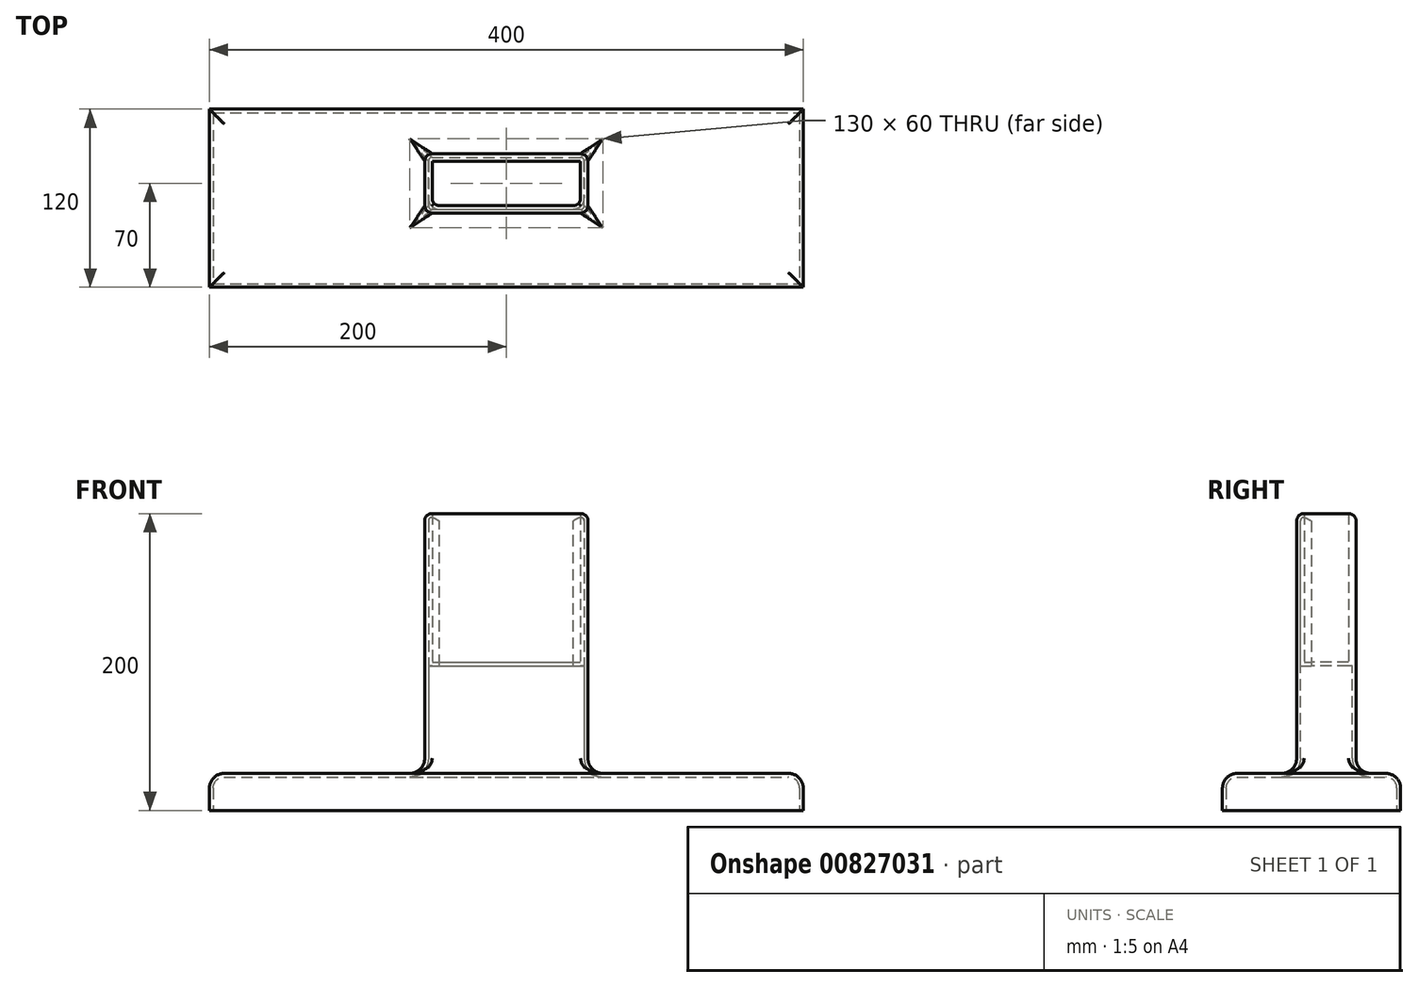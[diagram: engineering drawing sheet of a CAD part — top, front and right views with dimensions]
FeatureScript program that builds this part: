
annotation { "Feature Type Name" : "Feature", "Feature Type Description" : "" }
export const myFeature = defineFeature(function(context is Context, id is Id, definition is map)
    precondition{}
    {
        {
            var Q0;
            Q0=qCreatedBy(makeId("Front.planeOp"),FACE);
            var sketch = newSketch(context, id + "F0", { "sketchPlane" : qUnion([Q0])});
            skLineSegment(sketch, "E0.bottom", {"start": v(-55, 100) * mm, "end": v(55, 100) * mm});
            skLineSegment(sketch, "E0.top", {"start": v(-55, -100) * mm, "end": v(55, -100) * mm});
            skLineSegment(sketch, "E0.left", {"start": v(-55, 100) * mm, "end": v(-55, -100) * mm});
            skLineSegment(sketch, "E0.right", {"start": v(55, 100) * mm, "end": v(55, -100) * mm});
            skSolve(sketch);
        }
        {
            var Q0;
            Q0=makeQuery(id+"F0.imprint","IMPRINT",FACE,{"disambiguationData":[TD([[makeQuery(id+"F0.imprint","IMPRINT",EDGE,{"derivedFrom":sQuery(id+"F0.wireOp",EDGE,"E0.bottom")}),-1.0]])]});
            extrude(context, id + "F1", {"entities" : qUnion([Q0]), "depth" : 20 * mm, "offsetDistance" : 25 * mm, "hasSecondDirection" : true, "secondDirectionOppositeDirection" : true, "secondDirectionDepth" : 20 * mm});
        }
        {
            var Q0;
            Q0=qCreatedBy(makeId("Top.planeOp"),FACE);
            var sketch = newSketch(context, id + "F2", { "sketchPlane" : qUnion([Q0])});
            skLineSegment(sketch, "E1.bottom", {"start": v(-50, 15) * mm, "end": v(50, 15) * mm});
            skLineSegment(sketch, "E1.top", {"start": v(-50, -15) * mm, "end": v(50, -15) * mm});
            skLineSegment(sketch, "E1.left", {"start": v(-50, 15) * mm, "end": v(-50, -15) * mm});
            skLineSegment(sketch, "E1.right", {"start": v(50, 15) * mm, "end": v(50, -15) * mm});
            skSolve(sketch);
        }
        {
            var Q0;
            Q0 = qSketchRegion(id + "F2", true);
            extrude(context, id + "F3", {"entities" : qUnion([Q0]), "operationType" : NewBodyOperationType.REMOVE, "endBound" : BoundingType.UP_TO_NEXT, "depth" : 25 * mm, "offsetDistance" : 25 * mm});
        }
        {
            var Q0;
            Q0=qCreatedBy(makeId("Top.planeOp"),FACE);
            cPlane(context, id + "F4", {"entities" : qUnion([Q0]), "cplaneType" : CPlaneType.OFFSET, "offset" : 100 * mm, "oppositeDirection" : true, "width" : 150 * mm, "height" : 150 * mm});
        }
        {
            var Q0;
            Q0=qCreatedBy(id+"F4.planeOp",FACE);
            var sketch = newSketch(context, id + "F5", { "sketchPlane" : qUnion([Q0])});
            skLineSegment(sketch, "E2.bottom", {"start": v(70, 60) * mm, "end": v(-70, 60) * mm});
            skLineSegment(sketch, "E2.top", {"start": v(70, -60) * mm, "end": v(-70, -60) * mm});
            skLineSegment(sketch, "E2.left", {"start": v(70, 60) * mm, "end": v(70, -60) * mm});
            skLineSegment(sketch, "E2.right", {"start": v(-70, 60) * mm, "end": v(-70, -60) * mm});
            skLineSegment(sketch, "E3.bottom", {"start": v(-200, 50) * mm, "end": v(200, 50) * mm});
            skLineSegment(sketch, "E3.top", {"start": v(-200, -70) * mm, "end": v(200, -70) * mm});
            skLineSegment(sketch, "E3.left", {"start": v(-200, 50) * mm, "end": v(-200, -70) * mm});
            skLineSegment(sketch, "E3.right", {"start": v(200, 50) * mm, "end": v(200, -70) * mm});
            skSolve(sketch);
        }
        {
            var Q0;
            {var subQ0=sQuery(id+"F5.wireOp",EDGE,"E3.bottom");var subQ1=sQuery(id+"F5.wireOp",EDGE,"E2.left");var subQ2=makeQuery(id+"F5.imprint","INTERSECT",VERTEX,{"derivedFrom":[subQ1,subQ0]});Q0=makeQuery(id+"F5.imprint","IMPRINT",FACE,{"disambiguationData":[TD([[makeQuery(id+"F5.imprint","IMPRINT",EDGE,{"disambiguationData":[TD([[subQ2,-1.0]])],"derivedFrom":subQ1}),-1.0]])]});}
            var Q1;
            {var subQ5=sQuery(id+"F5.wireOp",EDGE,"E3.right");Q1=makeQuery(id+"F5.imprint","IMPRINT",FACE,{"disambiguationData":[TD([[makeQuery(id+"F5.imprint","IMPRINT",EDGE,{"derivedFrom":subQ5}),-1.0]])]});}
            var Q2;
            {var subQ5=sQuery(id+"F5.wireOp",EDGE,"E3.left");Q2=makeQuery(id+"F5.imprint","IMPRINT",FACE,{"disambiguationData":[TD([[makeQuery(id+"F5.imprint","IMPRINT",EDGE,{"derivedFrom":subQ5}),1.0]])]});}
            extrude(context, id + "F6", {"entities" : qUnion([Q0, Q1, Q2]), "operationType" : NewBodyOperationType.ADD, "depth" : 25 * mm, "offsetDistance" : 25 * mm});
        }
        {
            var Q0;
            Q0=makeQuery(id+"F6.boolean.opBoolean","INTERSECT",EDGE,{"derivedFrom":[makeQuery(id+"F1.opExtrude","CAP_FACE",FACE,{"disambiguationData":[OSD([sQuery(id+"F0.wireOp",EDGE,"E0.bottom"),sQuery(id+"F0.wireOp",EDGE,"E0.top"),sQuery(id+"F0.wireOp",EDGE,"E0.left"),sQuery(id+"F0.wireOp",EDGE,"E0.right")])],"isStart":false}),makeQuery(id+"F6.opExtrude","CAP_FACE",FACE,{"disambiguationData":[OSD([sQuery(id+"F5.wireOp",EDGE,"E3.bottom"),sQuery(id+"F5.wireOp",EDGE,"E3.top"),sQuery(id+"F5.wireOp",EDGE,"E3.left"),sQuery(id+"F5.wireOp",EDGE,"E3.right")])],"isStart":false})]});
            var Q1;
            Q1=makeQuery(id+"F6.boolean.opBoolean","INTERSECT",EDGE,{"derivedFrom":[makeQuery(id+"F1.opExtrude","SWEPT_FACE",FACE,{"disambiguationData":[OSD([sQuery(id+"F0.wireOp",EDGE,"E0.right")])]}),makeQuery(id+"F6.opExtrude","CAP_FACE",FACE,{"disambiguationData":[OSD([sQuery(id+"F5.wireOp",EDGE,"E3.bottom"),sQuery(id+"F5.wireOp",EDGE,"E3.top"),sQuery(id+"F5.wireOp",EDGE,"E3.left"),sQuery(id+"F5.wireOp",EDGE,"E3.right")])],"isStart":false})]});
            var Q2;
            Q2=makeQuery(id+"F6.boolean.opBoolean","INTERSECT",EDGE,{"derivedFrom":[makeQuery(id+"F1.opExtrude","CAP_FACE",FACE,{"disambiguationData":[OSD([sQuery(id+"F0.wireOp",EDGE,"E0.bottom"),sQuery(id+"F0.wireOp",EDGE,"E0.top"),sQuery(id+"F0.wireOp",EDGE,"E0.left"),sQuery(id+"F0.wireOp",EDGE,"E0.right")])],"isStart":true}),makeQuery(id+"F6.opExtrude","CAP_FACE",FACE,{"disambiguationData":[OSD([sQuery(id+"F5.wireOp",EDGE,"E3.bottom"),sQuery(id+"F5.wireOp",EDGE,"E3.top"),sQuery(id+"F5.wireOp",EDGE,"E3.left"),sQuery(id+"F5.wireOp",EDGE,"E3.right")])],"isStart":false})]});
            var Q3;
            Q3=makeQuery(id+"F6.boolean.opBoolean","INTERSECT",EDGE,{"derivedFrom":[makeQuery(id+"F1.opExtrude","SWEPT_FACE",FACE,{"disambiguationData":[OSD([sQuery(id+"F0.wireOp",EDGE,"E0.left")])]}),makeQuery(id+"F6.opExtrude","CAP_FACE",FACE,{"disambiguationData":[OSD([sQuery(id+"F5.wireOp",EDGE,"E3.bottom"),sQuery(id+"F5.wireOp",EDGE,"E3.top"),sQuery(id+"F5.wireOp",EDGE,"E3.left"),sQuery(id+"F5.wireOp",EDGE,"E3.right")])],"isStart":false})]});
            var Q4;
            Q4=makeQuery(id+"F6.opExtrude","CAP_FACE",FACE,{"disambiguationData":[OSD([sQuery(id+"F5.wireOp",EDGE,"E3.bottom"),sQuery(id+"F5.wireOp",EDGE,"E3.top"),sQuery(id+"F5.wireOp",EDGE,"E3.left"),sQuery(id+"F5.wireOp",EDGE,"E3.right")])],"isStart":false});
            fillet(context, id + "F7", {"entities" : qUnion([Q0, Q1, Q2, Q3, Q4]), "radius" : 10 * mm, "tangentPropagation" : true, "allowEdgeOverflow" : false});
        }
        {
            var Q0;
            Q0=makeQuery(id+"F1.opExtrude","CAP_EDGE",EDGE,{"disambiguationData":[OSD([sQuery(id+"F0.wireOp",EDGE,"E0.right")])],"isStart":true});
            var Q1;
            Q1=makeQuery(id+"F1.opExtrude","CAP_EDGE",EDGE,{"disambiguationData":[OSD([sQuery(id+"F0.wireOp",EDGE,"E0.right")])],"isStart":false});
            var Q2;
            Q2=makeQuery(id+"F1.opExtrude","CAP_EDGE",EDGE,{"disambiguationData":[OSD([sQuery(id+"F0.wireOp",EDGE,"E0.left")])],"isStart":true});
            var Q3;
            Q3=makeQuery(id+"F1.opExtrude","CAP_EDGE",EDGE,{"disambiguationData":[OSD([sQuery(id+"F0.wireOp",EDGE,"E0.left")])],"isStart":false});
            var Q4;
            Q4=makeQuery(id+"F1.opExtrude","SWEPT_EDGE",EDGE,{"disambiguationData":[OSD([sQuery(id+"F0.wireOp",EDGE,"E0.bottom"),sQuery(id+"F0.wireOp",EDGE,"E0.right")])]});
            var Q5;
            Q5=makeQuery(id+"F1.opExtrude","CAP_EDGE",EDGE,{"disambiguationData":[OSD([sQuery(id+"F0.wireOp",EDGE,"E0.bottom")])],"isStart":true});
            var Q6;
            Q6=makeQuery(id+"F1.opExtrude","CAP_EDGE",EDGE,{"disambiguationData":[OSD([sQuery(id+"F0.wireOp",EDGE,"E0.bottom")])],"isStart":false});
            var Q7;
            Q7=makeQuery(id+"F1.opExtrude","SWEPT_EDGE",EDGE,{"disambiguationData":[OSD([sQuery(id+"F0.wireOp",EDGE,"E0.bottom"),sQuery(id+"F0.wireOp",EDGE,"E0.left")])]});
            fillet(context, id + "F8", {"entities" : qUnion([Q0, Q1, Q2, Q3, Q4, Q5, Q6, Q7]), "radius" : 5 * mm, "tangentPropagation" : true, "allowEdgeOverflow" : false});
        }
        {
            var Q0;
            Q0=makeQuery(id+"F3.boolean.opBoolean","COPY",EDGE,{"derivedFrom":makeQuery(id+"F3.opExtrude","SWEPT_EDGE",EDGE,{"disambiguationData":[OSD([sQuery(id+"F2.wireOp",EDGE,"E1.top"),sQuery(id+"F2.wireOp",EDGE,"E1.left")])]})});
            var Q1;
            Q1=makeQuery(id+"F3.boolean.opBoolean","COPY",EDGE,{"derivedFrom":makeQuery(id+"F3.opExtrude","SWEPT_EDGE",EDGE,{"disambiguationData":[OSD([sQuery(id+"F2.wireOp",EDGE,"E1.top"),sQuery(id+"F2.wireOp",EDGE,"E1.right")])]})});
            fillet(context, id + "F9", {"entities" : qUnion([Q0, Q1]), "radius" : 5 * mm, "tangentPropagation" : true, "allowEdgeOverflow" : false});
        }
        {
            var Q0;
            Q0=makeQuery(id+"F6.boolean.opBoolean","MERGE",FACE,{"derivedFrom":[makeQuery(id+"F1.opExtrude","SWEPT_FACE",FACE,{"disambiguationData":[OSD([sQuery(id+"F0.wireOp",EDGE,"E0.top")])]}),makeQuery(id+"F6.opExtrude","CAP_FACE",FACE,{"disambiguationData":[OSD([sQuery(id+"F5.wireOp",EDGE,"E3.bottom"),sQuery(id+"F5.wireOp",EDGE,"E3.top"),sQuery(id+"F5.wireOp",EDGE,"E3.left"),sQuery(id+"F5.wireOp",EDGE,"E3.right")])],"isStart":true})]});
            shell(context, id + "F10", {"entities" : qUnion([Q0]), "thickness" : 2.5 * mm});
        }
    });
